# Revit family: Haworth_Very_Chair_ConferencePerforated
name_source: partatom
category: Furniture
revit_build: Autodesk Revit 2018 (Build: 20170223_1515(x64)
units: mm (PartAtom-declared; Revit-internal decimal feet)

## family parameters
Always vertical = Yes
Cut with Voids When Loaded = No
OmniClass Number = 23.40.70.14.64.21
OmniClass Title = Systems Furniture
Room Calculation Point = No
Shared = No
Work Plane-Based = No

## types (2) — shared parameters
Actual Depth = 26 179/256"
Actual Height = 36 115/128"
Actual Width = 21 205/256"
Arm Cap Finish = Haworth _ Polymer _ Slate
Assembly Code = E2020200
Back Cushion = No
Back Finish = Haworth _ Polymer _ Glacier
Chair Finish = Haworth _ Polymer _ Glacier
Cushion Finish = Haworth _ Fabric _ Tellure _ Sky 3A-32
Depth = 28"
Description = Perforated Conference
Frame Finish = Haworth _ Metal _ Chrome
Manufacturer = Haworth
Model = Haworth - Chair - Very
Revision Number = 3
Seat Cushion = No
Size = Verify Final Dim. w/ Haworth
Sustainability Info = https://www.haworth.com
URL = www.haworth.com
URL - Product = http://www.haworth.com
Warranty = http://www.haworth.com

## per-type parameters (varying)
| type | Arms |
| Arms | Yes |
| No Arms | No |

## geometry (parser evidence)
native form markers: Blend x26, Sweep x8
no freeform markers — native parametric forms only
